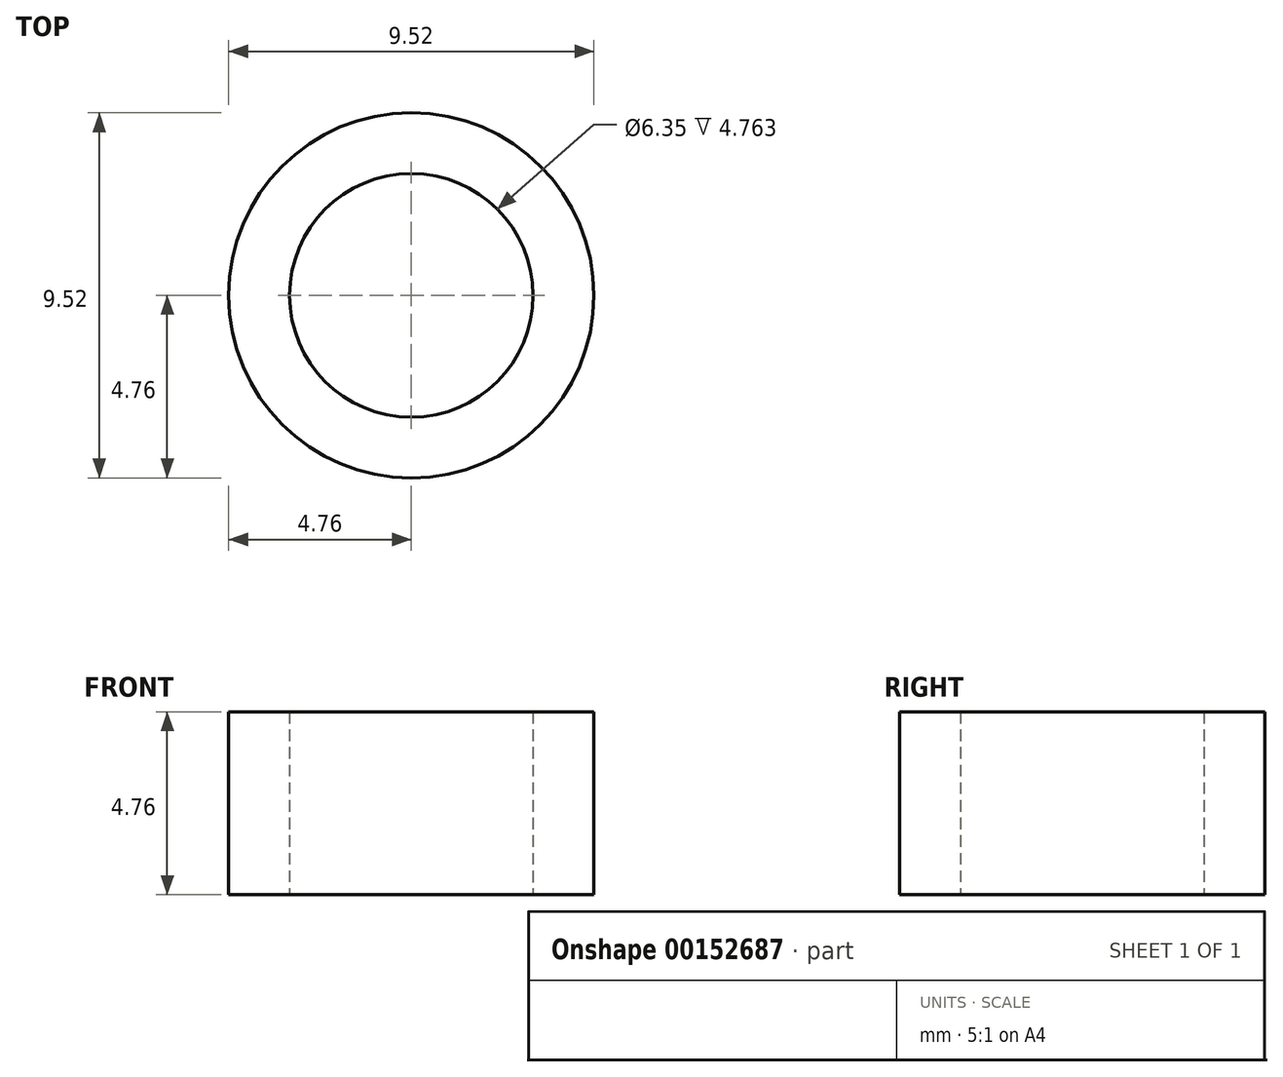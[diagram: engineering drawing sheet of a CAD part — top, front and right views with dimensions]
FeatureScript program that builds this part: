
annotation { "Feature Type Name" : "Feature", "Feature Type Description" : "" }
export const myFeature = defineFeature(function(context is Context, id is Id, definition is map)
    precondition{}
    {
        {
            var Q0;
            Q0=qCreatedBy(makeId("Top.planeOp"),FACE);
            var sketch = newSketch(context, id + "F0", { "sketchPlane" : qUnion([Q0])});
            skCircle(sketch, "E0", {"center": v(0, 0) * mm, "radius": 3.18 * mm});
            skCircle(sketch, "E1", {"center": v(0, 0) * mm, "radius": 4.76 * mm});
            skSolve(sketch);
        }
        {
            var Q0;
            Q0=qSketchRegion(id+"F0",true);
            extrude(context, id + "F1", {"entities" : qUnion([Q0]), "depth" : 4.76 * mm});
        }
    });
